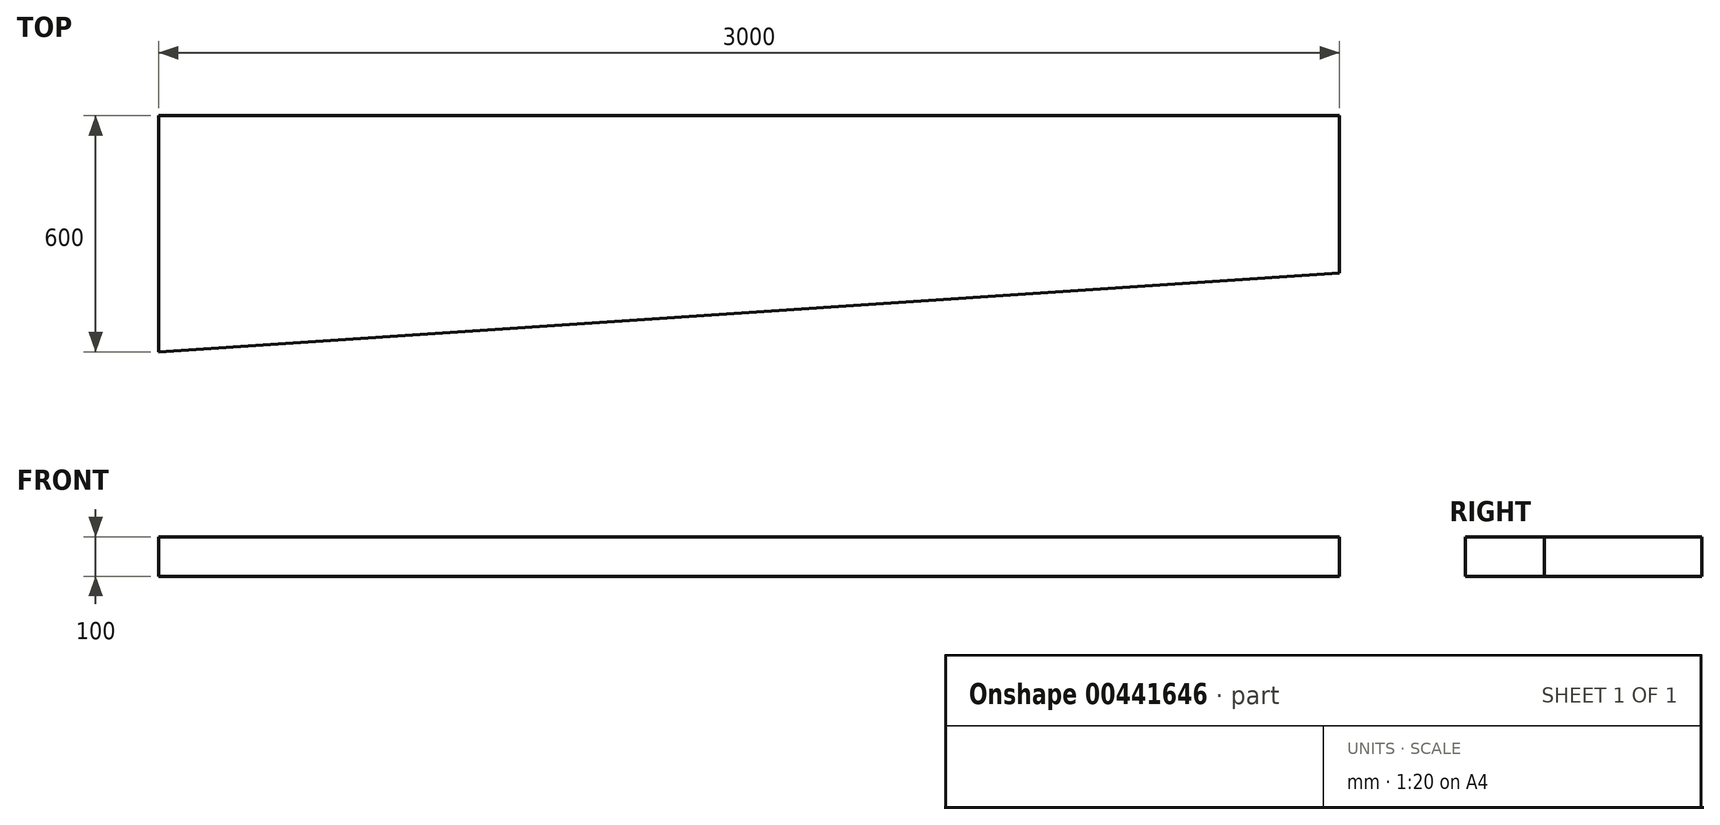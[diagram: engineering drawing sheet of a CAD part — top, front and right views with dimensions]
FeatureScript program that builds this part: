
annotation { "Feature Type Name" : "Feature", "Feature Type Description" : "" }
export const myFeature = defineFeature(function(context is Context, id is Id, definition is map)
    precondition{}
    {
        {
            var Q0;
            Q0=qCreatedBy(makeId("Top.planeOp"),FACE);
            var sketch = newSketch(context, id + "F0", { "sketchPlane" : qUnion([Q0])});
            skLineSegment(sketch, "E0", {"start": v(0, 0) * mm, "end": v(0, -600) * mm});
            skLineSegment(sketch, "E1", {"start": v(0, -600) * mm, "end": v(3000, -400) * mm});
            skLineSegment(sketch, "E2", {"start": v(3000, -400) * mm, "end": v(3000, 0) * mm});
            skLineSegment(sketch, "E3", {"start": v(3000, 0) * mm, "end": v(0, 0) * mm});
            skSolve(sketch);
        }
        {
            var Q0;
            Q0 = qSketchRegion(id + "F0", true);
            extrude(context, id + "F1", {"entities" : qUnion([Q0]), "depth" : 100 * mm, "offsetDistance" : 25 * mm});
        }
    });
